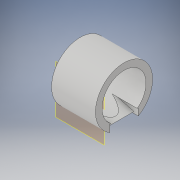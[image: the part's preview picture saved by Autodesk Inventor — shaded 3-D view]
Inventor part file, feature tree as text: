
AUTODESK INVENTOR PART (.ipt)
format: ipt  version: 2019 (Build 230136000, 136)  size: 129,536 bytes
history: native  units: in
note: dims shown in document units (in); Inventor stores cm internally (conversion verified against a paired STEP export)
features: sketch x2, plane x1, revolve x1, extrude x1
ambient origin geometry x8: Origin, YZ Plane, XZ Plane, XY Plane, X Axis, Y Axis, Z Axis, Center Point
bodies: Solid1 (feature_tree)
feature tree (5):
  plane  "Work Plane1"
  revolve  "Revolution1"  [1 undecoded]
  extrude  "Extrusion2"  TaperAngle=90.0deg  [1 undecoded]
  sketch  "Sketch2"  dims[d11=0.7874in d12=0.1181in]
  sketch  "Sketch3"  dims[d13=0.3937in d15=90.0deg d17=0.6693in d19=15.0deg d20=15.0deg d21=0.0984in d23=0.7087in d24=0.1969in d25=0.2091in d26=0.302in d27=0.5118in d28=0.0in]
note: 2 required parameter values undecoded (feature->parameter linkage not recoverable at this tier; creation-order binding heuristic only, values carry confidence <= 0.55)